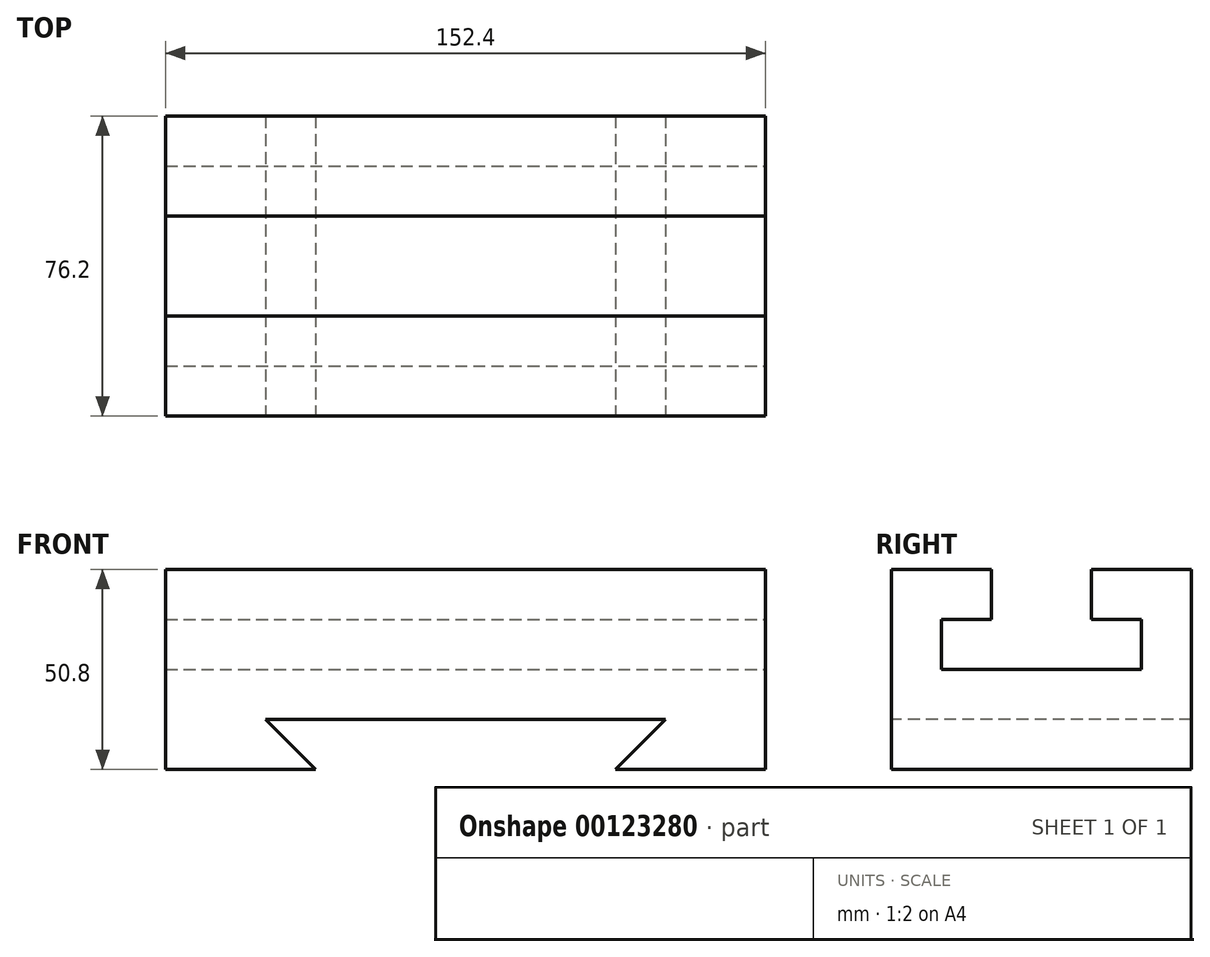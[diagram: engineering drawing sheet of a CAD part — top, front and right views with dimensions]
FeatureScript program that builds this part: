
annotation { "Feature Type Name" : "Feature", "Feature Type Description" : "" }
export const myFeature = defineFeature(function(context is Context, id is Id, definition is map)
    precondition{}
    {
        {
            var Q0;
            Q0=qCreatedBy(makeId("Front.planeOp"),FACE);
            var sketch = newSketch(context, id + "F0", { "sketchPlane" : qUnion([Q0])});
            skLineSegment(sketch, "E0.bottom", {"start": v(76.2, 25.4) * mm, "end": v(-76.2, 25.4) * mm});
            skLineSegment(sketch, "E0.top", {"start": v(76.2, -25.4) * mm, "end": v(-76.2, -25.4) * mm});
            skLineSegment(sketch, "E0.left", {"start": v(76.2, 25.4) * mm, "end": v(76.2, -25.4) * mm});
            skLineSegment(sketch, "E0.right", {"start": v(-76.2, 25.4) * mm, "end": v(-76.2, -25.4) * mm});
            skPoint(sketch, "E0.middle", {"position": v(0, 0) * mm});
            skSolve(sketch);
        }
        {
            var Q0;
            Q0 = qSketchRegion(id + "F0", true);
            extrude(context, id + "F1", {"entities" : qUnion([Q0]), "depth" : 76.2 * mm});
        }
        {
            var Q0;
            Q0=makeQuery(id+"F1.opExtrude","SWEPT_FACE",FACE,{"disambiguationData":[OSD([sQuery(id+"F0.wireOp",EDGE,"E0.left")])]});
            var sketch = newSketch(context, id + "F2", { "sketchPlane" : qUnion([Q0])});
            skLineSegment(sketch, "E1", {"start": v(0, 25.4) * mm, "end": v(-25.4, 25.4) * mm});
            skLineSegment(sketch, "E2", {"start": v(-25.4, 25.4) * mm, "end": v(-25.4, 12.7) * mm});
            skLineSegment(sketch, "E3", {"start": v(-25.4, 12.7) * mm, "end": v(-12.7, 12.7) * mm});
            skLineSegment(sketch, "E4", {"start": v(-12.7, 12.7) * mm, "end": v(-12.7, 0) * mm});
            skLineSegment(sketch, "E5", {"start": v(-12.7, 0) * mm, "end": v(-63.5, 0) * mm});
            skLineSegment(sketch, "E6", {"start": v(-63.5, 0) * mm, "end": v(-63.5, 12.7) * mm});
            skLineSegment(sketch, "E7", {"start": v(-63.5, 12.7) * mm, "end": v(-50.8, 12.7) * mm});
            skLineSegment(sketch, "E8", {"start": v(-50.8, 12.7) * mm, "end": v(-50.8, 25.4) * mm});
            skLineSegment(sketch, "E9", {"start": v(-50.8, 25.4) * mm, "end": v(-25.4, 25.4) * mm});
            skSolve(sketch);
        }
        {
            var Q0;
            Q0=makeQuery(id+"F2.imprint","IMPRINT",FACE,{"disambiguationData":[TD([[makeQuery(id+"F2.imprint","IMPRINT",EDGE,{"derivedFrom":sQuery(id+"F2.wireOp",EDGE,"E2")}),-1.0]])]});
            extrude(context, id + "F3", {"entities" : qUnion([Q0]), "operationType" : NewBodyOperationType.REMOVE, "endBound" : BoundingType.THROUGH_ALL, "oppositeDirection" : true, "depth" : 25.4 * mm});
        }
        {
            var Q0;
            Q0=makeQuery(id+"F1.opExtrude","CAP_FACE",FACE,{"disambiguationData":[OSD([sQuery(id+"F0.wireOp",EDGE,"E0.bottom"),sQuery(id+"F0.wireOp",EDGE,"E0.top"),sQuery(id+"F0.wireOp",EDGE,"E0.left"),sQuery(id+"F0.wireOp",EDGE,"E0.right")])],"isStart":false});
            var sketch = newSketch(context, id + "F4", { "sketchPlane" : qUnion([Q0])});
            skLineSegment(sketch, "E10", {"start": v(0, -12.7) * mm, "end": v(50.8, -12.7) * mm});
            skLineSegment(sketch, "E11", {"start": v(0, -12.7) * mm, "end": v(-50.8, -12.7) * mm});
            skLineSegment(sketch, "E12", {"start": v(-50.8, -12.7) * mm, "end": v(-38.1, -25.4) * mm});
            skLineSegment(sketch, "E13", {"start": v(38.1, -25.4) * mm, "end": v(50.8, -12.7) * mm});
            skLineSegment(sketch, "E14", {"start": v(-38.1, -25.4) * mm, "end": v(38.1, -25.4) * mm});
            skSolve(sketch);
        }
        {
            var Q0;
            Q0=makeQuery(id+"F4.imprint","IMPRINT",FACE,{"disambiguationData":[TD([[makeQuery(id+"F4.imprint","IMPRINT",EDGE,{"derivedFrom":sQuery(id+"F4.wireOp",EDGE,"E10")}),-1.0]])]});
            extrude(context, id + "F5", {"entities" : qUnion([Q0]), "operationType" : NewBodyOperationType.REMOVE, "endBound" : BoundingType.THROUGH_ALL, "oppositeDirection" : true, "depth" : 25.4 * mm});
        }
    });
